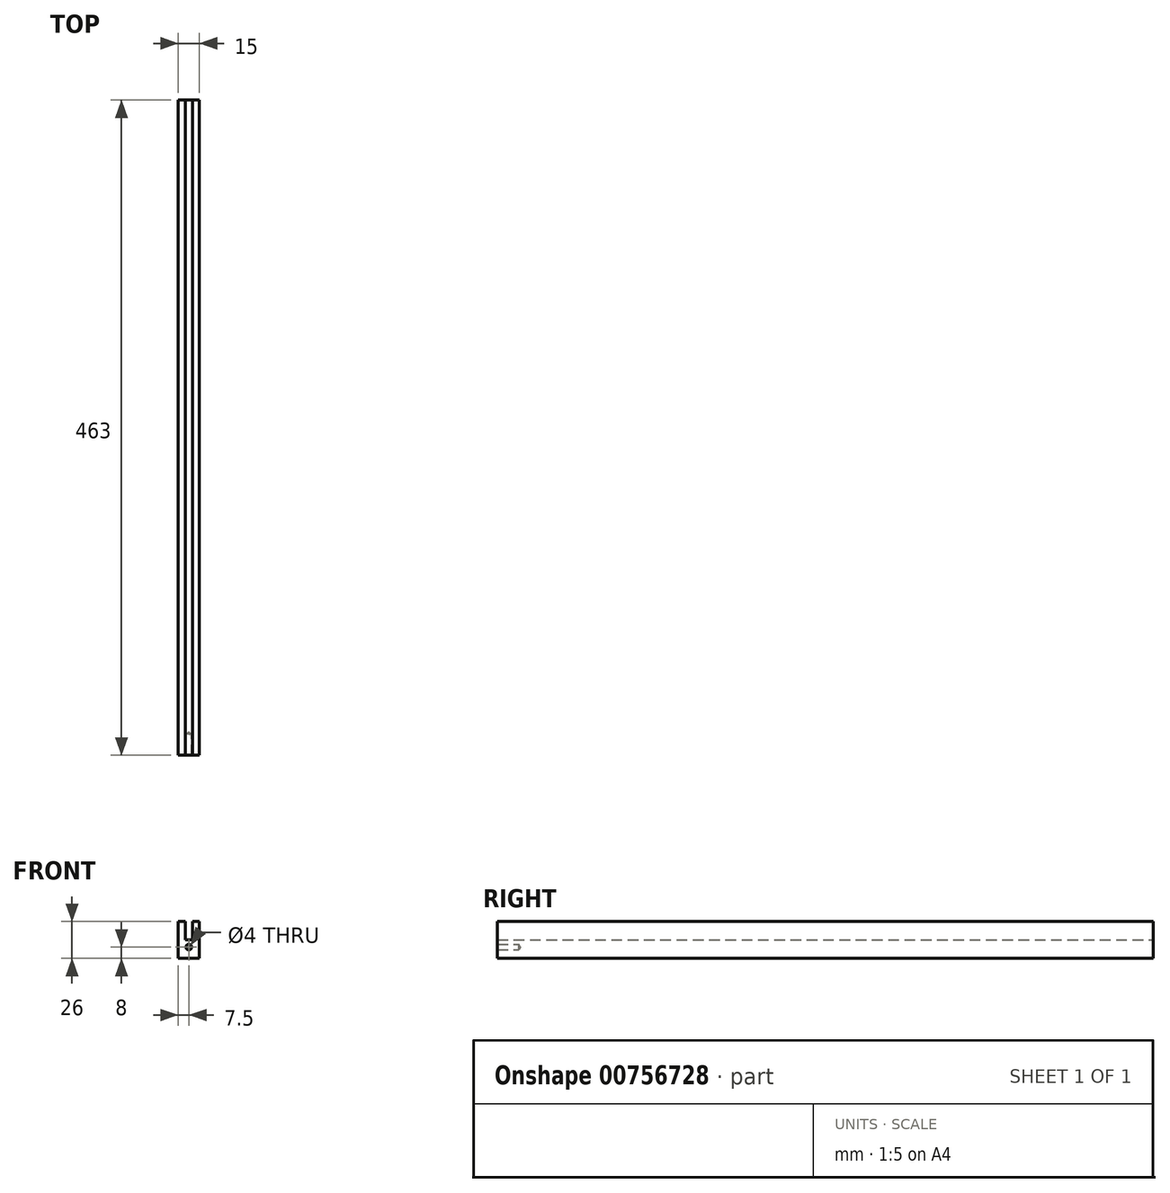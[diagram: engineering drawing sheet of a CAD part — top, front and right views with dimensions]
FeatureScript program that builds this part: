
annotation { "Feature Type Name" : "Feature", "Feature Type Description" : "" }
export const myFeature = defineFeature(function(context is Context, id is Id, definition is map)
    precondition{}
    {
        {
            var Q0;
            Q0=qCreatedBy(makeId("Front.planeOp"),FACE);
            var sketch = newSketch(context, id + "F0", { "sketchPlane" : qUnion([Q0])});
            skLineSegment(sketch, "E0", {"start": v(7.5, 0) * mm, "end": v(-7.5, 0) * mm});
            skLineSegment(sketch, "E1", {"start": v(-7.5, 0) * mm, "end": v(-7.5, 26) * mm});
            skLineSegment(sketch, "E2", {"start": v(-7.5, 26) * mm, "end": v(-2.5, 26) * mm});
            skLineSegment(sketch, "E3", {"start": v(-2.5, 26) * mm, "end": v(-2.5, 13) * mm});
            skLineSegment(sketch, "E4", {"start": v(-2.5, 13) * mm, "end": v(2.5, 13) * mm});
            skLineSegment(sketch, "E5", {"start": v(2.5, 13) * mm, "end": v(2.5, 26) * mm});
            skLineSegment(sketch, "E6", {"start": v(2.5, 26) * mm, "end": v(7.5, 26) * mm});
            skLineSegment(sketch, "E7", {"start": v(7.5, 26) * mm, "end": v(7.5, 0) * mm});
            skSolve(sketch);
        }
        {
            var Q0;
            Q0=makeQuery(id+"F0.imprint","IMPRINT",FACE,{"disambiguationData":[TD([[makeQuery(id+"F0.imprint","IMPRINT",EDGE,{"derivedFrom":sQuery(id+"F0.wireOp",EDGE,"E0")}),-1.0]])]});
            extrude(context, id + "F1", {"entities" : qUnion([Q0]), "depth" : (473 - 10) * mm, "offsetDistance" : 25 * mm, "symmetric" : true});
        }
        {
            var Q0;
            Q0=makeQuery(id+"F1.opExtrude","CAP_FACE",FACE,{"disambiguationData":[OSD([sQuery(id+"F0.wireOp",EDGE,"E0"),sQuery(id+"F0.wireOp",EDGE,"E1"),sQuery(id+"F0.wireOp",EDGE,"E2"),sQuery(id+"F0.wireOp",EDGE,"E3"),sQuery(id+"F0.wireOp",EDGE,"E4"),sQuery(id+"F0.wireOp",EDGE,"E5"),sQuery(id+"F0.wireOp",EDGE,"E6"),sQuery(id+"F0.wireOp",EDGE,"E7")])],"isStart":false});
            var sketch = newSketch(context, id + "F2", { "sketchPlane" : qUnion([Q0])});
            skPoint(sketch, "E8", {"position": v(0, 8) * mm});
            skSolve(sketch);
        }
        {
            var Q0;
            Q0=sQuery(id+"F2.wireOp",VERTEX,"E8");
            var Q1;
            Q1=makeQuery(id+"F1.opExtrude","SWEPT_BODY",BODY,{"disambiguationData":[OSD([sQuery(id+"F0.wireOp",EDGE,"E0"),sQuery(id+"F0.wireOp",EDGE,"E1"),sQuery(id+"F0.wireOp",EDGE,"E2"),sQuery(id+"F0.wireOp",EDGE,"E3"),sQuery(id+"F0.wireOp",EDGE,"E4"),sQuery(id+"F0.wireOp",EDGE,"E5"),sQuery(id+"F0.wireOp",EDGE,"E6"),sQuery(id+"F0.wireOp",EDGE,"E7")])]});
            hole(context, id + "F3", {"style" : HoleStyle.SIMPLE, "endStyle" : HoleEndStyle.BLIND, "holeDiameter" : 4 * mm, "majorDiameter" : 5 * mm, "holeDepth" : 15 * mm, "isTappedThrough" : true, "tappedDepth" : 12 * mm, "tapClearance" : 3, "locations" : qUnion([Q0]), "scope" : qUnion([Q1])});
        }
    });
